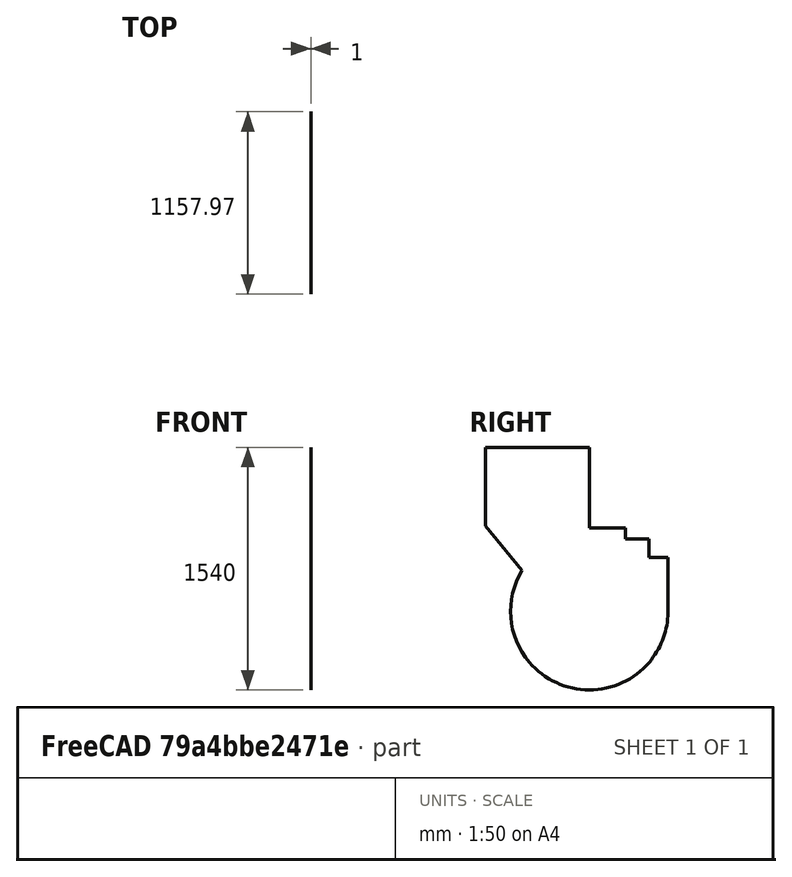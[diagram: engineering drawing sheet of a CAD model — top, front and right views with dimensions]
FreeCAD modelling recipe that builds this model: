
FCSTD DOCUMENT
Label: Shell_front_no_bin
objects: Sketcher::SketchObject×1, PartDesign::Pad×1
note: 3 computed .brp shape members not serialized (recipe doc carries the construction recipe); baked Part::Feature solids carry a one-line shape summary decoded from their .brp

FEATURE [Sketcher::SketchObject] Sketch  label="Shell_front"
  Placement = pos=(500,0,0) rot=(0.57735,0.57735,0.57735;2.0944rad)
  sketch-geometry (13):
    g0: ArcOfCircle CenterX=0 CenterY=0 CenterZ=0 NormalX=0 NormalY=0 NormalZ=1 Radius=500 StartAngle=2.59474 EndAngle=3.84621
    g1: LineSegment StartX=-427.083 StartY=260 StartZ=0 EndX=-658.874 EndY=540 EndZ=0
    g2: LineSegment StartX=0 StartY=530 StartZ=0 EndX=230 EndY=530 EndZ=0
    g3: LineSegment StartX=230 StartY=530 StartZ=0 EndX=230 EndY=460 EndZ=0
    g4: LineSegment StartX=230 StartY=460 StartZ=0 EndX=380 EndY=460 EndZ=0
    g5: LineSegment StartX=380 StartY=460 StartZ=0 EndX=380 EndY=340 EndZ=0
    g6: LineSegment StartX=380 StartY=340 StartZ=0 EndX=499.099 EndY=340 EndZ=0
    g7: LineSegment StartX=499.099 StartY=340 StartZ=0 EndX=499.099 EndY=-30 EndZ=0
    g8: LineSegment StartX=-658.874 StartY=1040 StartZ=0 EndX=-658.874 EndY=540 EndZ=0
    g9: ArcOfCircle CenterX=0 CenterY=0 CenterZ=0 NormalX=0 NormalY=0 NormalZ=1 Radius=500 StartAngle=5.57857 EndAngle=6.22315
    g10: LineSegment StartX=-658.874 StartY=1040 StartZ=0 EndX=0 EndY=1040 EndZ=0
    g11: LineSegment StartX=0 StartY=1040 StartZ=0 EndX=0 EndY=530 EndZ=0
    g12: ArcOfCircle CenterX=0 CenterY=0 CenterZ=0 NormalX=0 NormalY=0 NormalZ=1 Radius=500 StartAngle=3.84621 EndAngle=5.57857
  constraints (40):
    c: Radius(g0) = 500
    c: DistanceX(g0) = 0
    c: DistanceY(g0) = 0
    c: Horizontal(g2)
    c: Vertical(g3)
    c: Coincident(g4,g3)
    c: Horizontal(g4)
    c: Vertical(g5)
    c: Coincident(g6,g5)
    c: Horizontal(g6)
    c: DistanceY(g1) = 540
    c: Coincident(g2,g3)
    c: Coincident(g4,g5)
    c: Coincident(g7,g9)
    c: Vertical(g7)
    c: Distance(g7) = 370
    c: Coincident(g1,g0)
    c: Coincident(g8,g1)
    c: Vertical(g8)
    c: Distance(g1) = 363.493
    c: Distance(g8) = 500
    c: Coincident(g0,g9)
    c: Coincident(g10,g8)
    c: Horizontal(g10)
    c: Coincident(g11,g10)
    c: Vertical(g11)
    c: Coincident(g6,g7)
    c: Coincident(g11,g2)
    c: DistanceX(g5) = 380
    c: DistanceY(g5) = 340
    c: DistanceX(g3) = 230
    c: DistanceY(g3) = 460
    c: DistanceX(g2) = 0
    c: DistanceY(g2) = 530
    c: DistanceY(g0) = 260
    c: Radius(g9) = 500
    c: Coincident(g12,g0)
    c: Coincident(g12,g0)
    c: DistanceY(g0) = -323.87
    c: DistanceY(g9) = -323.87
FEATURE [PartDesign::Pad] Pad  label="Shell_front_"
  Length = 1
  MirroredExtent = false
  Sketch = -> Sketch
